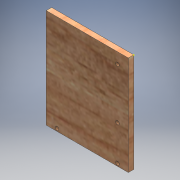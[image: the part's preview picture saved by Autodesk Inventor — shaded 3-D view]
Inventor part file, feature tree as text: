
AUTODESK INVENTOR PART (.ipt)
format: ipt  version: 2016 (Build 200138000, 138)  size: 131,584 bytes
history: native  units: mm
features: sketch x3, extrude x1, hole x1
ambient origin geometry x8: Origin, YZ Plane, XZ Plane, XY Plane, X Axis, Y Axis, Z Axis, Center Point
bodies: Solid1 (feature_tree)
feature tree (5):
  extrude  "Extrusion1"  Depth=55.0mm
  hole  "Hole1"  [1 undecoded]
  sketch  "Sketch3"  dims[d5=2.0mm d6=6.0mm d7=6.0mm d8=2.0mm d9=6.0mm d10=6.0mm d11=2.0mm d12=6.0mm d13=4.0mm d14=2.0mm d15=90.0deg d16=8.0mm d17=20.594885mm d18=3.0mm d19=1.0mm d20=6.0mm]
  sketch  "Sketch1"  dims[d0=45.5mm d1=55.0mm]
  sketch  "Sketch2"  dims[d2=3.0mm d3=0.0mm d4=15.0mm]
note: 1 required parameter value undecoded (feature->parameter linkage not recoverable at this tier; creation-order binding heuristic only, values carry confidence <= 0.55)
